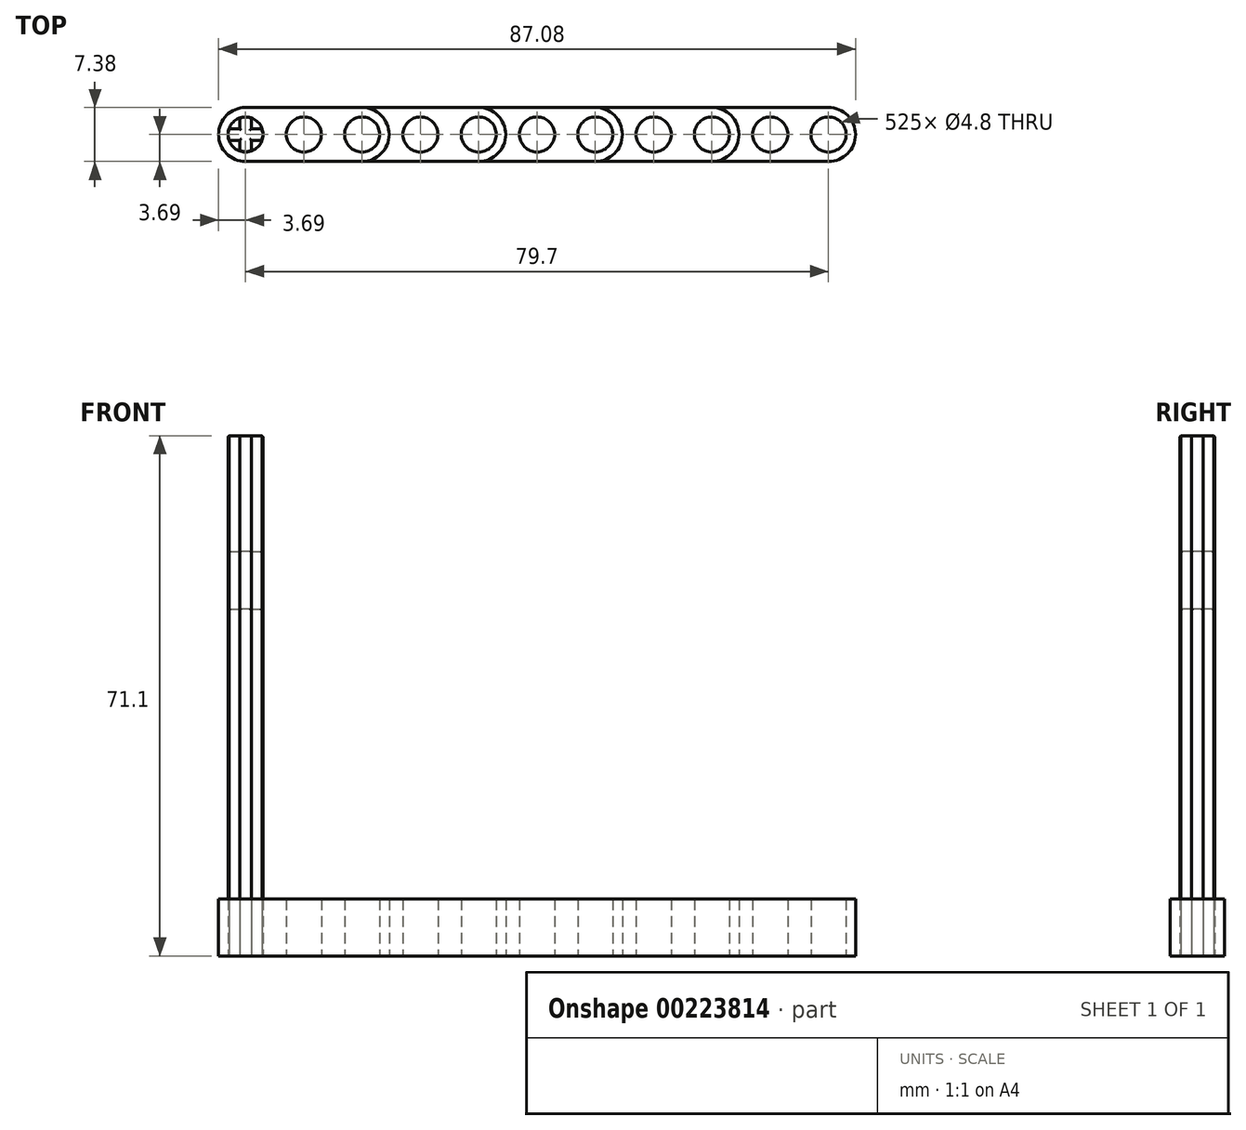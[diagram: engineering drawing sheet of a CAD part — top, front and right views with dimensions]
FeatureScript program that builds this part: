
annotation { "Feature Type Name" : "Feature", "Feature Type Description" : "" }
export const myFeature = defineFeature(function(context is Context, id is Id, definition is map)
    precondition{}
    {
        {
            var Q0;
            Q0=qCreatedBy(makeId("Top.planeOp"),FACE);
            var sketch = newSketch(context, id + "F0", { "sketchPlane" : qUnion([Q0])});
            skLineSegment(sketch, "E0", {"start": v(0, 0) * mm, "end": v(15.94, 0) * mm, "construction": true});
            skArc(sketch, "E1", {"start": v(15.94, -3.7) * mm, "mid": v(19.63, 0) * mm, "end": v(15.94, 3.69) * mm});
            skArc(sketch, "E2", {"start": v(0, 3.7) * mm, "mid": v(-3.7, 0) * mm, "end": v(0, -3.7) * mm});
            skLineSegment(sketch, "E3.MirrorCS", {"start": v(0, 3.69) * mm, "end": v(15.94, 3.69) * mm});
            skLineSegment(sketch, "E4.MirrorCS", {"start": v(0, -3.69) * mm, "end": v(15.94, -3.69) * mm});
            skCircle(sketch, "E5", {"center": v(0, 0) * mm, "radius": 2.4 * mm});
            skCircle(sketch, "E6.1.0.0", {"center": v(7.97, 0) * mm, "radius": 2.4 * mm});
            skCircle(sketch, "E6.2.0.0", {"center": v(15.94, 0) * mm, "radius": 2.4 * mm});
            skLineSegment(sketch, "E6.direction1", {"start": v(0, 0) * mm, "end": v(7.97, 0) * mm, "construction": true});
            skCircle(sketch, "E7", {"center": v(0, 0) * mm, "radius": 3.1 * mm});
            skCircle(sketch, "E8.1.0.0", {"center": v(7.97, 0) * mm, "radius": 3.1 * mm});
            skCircle(sketch, "E8.2.0.0", {"center": v(15.94, 0) * mm, "radius": 3.1 * mm});
            skSolve(sketch);
        }
        {
            var Q0;
            Q0=qCreatedBy(makeId("Top.planeOp"),FACE);
            var sketch = newSketch(context, id + "F1", { "sketchPlane" : qUnion([Q0])});
            skLineSegment(sketch, "E9", {"start": v(0, 0) * mm, "end": v(31.88, 0) * mm, "construction": true});
            skArc(sketch, "E10", {"start": v(31.88, -3.7) * mm, "mid": v(35.57, 0) * mm, "end": v(31.88, 3.7) * mm});
            skArc(sketch, "E11", {"start": v(0, 3.7) * mm, "mid": v(-3.7, 0) * mm, "end": v(0, -3.7) * mm});
            skLineSegment(sketch, "E12", {"start": v(0, 3.7) * mm, "end": v(31.88, 3.7) * mm});
            skLineSegment(sketch, "E13.MirrorCS", {"start": v(0, -3.7) * mm, "end": v(31.88, -3.7) * mm});
            skCircle(sketch, "E14", {"center": v(0, 0) * mm, "radius": 2.4 * mm});
            skCircle(sketch, "E15.1.0.0", {"center": v(7.97, 0) * mm, "radius": 2.4 * mm});
            skCircle(sketch, "E15.2.0.0", {"center": v(15.94, 0) * mm, "radius": 2.4 * mm});
            skCircle(sketch, "E15.3.0.0", {"center": v(23.91, 0) * mm, "radius": 2.4 * mm});
            skCircle(sketch, "E15.4.0.0", {"center": v(31.88, 0) * mm, "radius": 2.4 * mm});
            skLineSegment(sketch, "E15.direction1", {"start": v(0, 0) * mm, "end": v(7.97, 0) * mm, "construction": true});
            skSolve(sketch);
        }
        {
            var Q0;
            Q0=qCreatedBy(makeId("Top.planeOp"),FACE);
            var sketch = newSketch(context, id + "F17", { "sketchPlane" : qUnion([Q0])});
            skArc(sketch, "E16", {"start": v(47.82, -3.7) * mm, "mid": v(51.51, 0) * mm, "end": v(47.82, 3.7) * mm});
            skArc(sketch, "E17", {"start": v(0, 3.7) * mm, "mid": v(-3.7, 0) * mm, "end": v(0, -3.7) * mm});
            skLineSegment(sketch, "E18.MirrorCS", {"start": v(0, 3.7) * mm, "end": v(47.82, 3.7) * mm});
            skLineSegment(sketch, "E19.MirrorCS", {"start": v(0, -3.7) * mm, "end": v(47.82, -3.7) * mm});
            skCircle(sketch, "E20", {"center": v(0, 0) * mm, "radius": 2.4 * mm});
            skCircle(sketch, "E21.1.0.0", {"center": v(7.97, 0) * mm, "radius": 2.4 * mm});
            skCircle(sketch, "E21.2.0.0", {"center": v(15.94, 0) * mm, "radius": 2.4 * mm});
            skCircle(sketch, "E21.3.0.0", {"center": v(23.91, 0) * mm, "radius": 2.4 * mm});
            skCircle(sketch, "E21.4.0.0", {"center": v(31.88, 0) * mm, "radius": 2.4 * mm});
            skCircle(sketch, "E21.5.0.0", {"center": v(39.85, 0) * mm, "radius": 2.4 * mm});
            skCircle(sketch, "E21.6.0.0", {"center": v(47.82, 0) * mm, "radius": 2.4 * mm});
            skLineSegment(sketch, "E21.direction1", {"start": v(0, 0) * mm, "end": v(7.97, 0) * mm, "construction": true});
            skSolve(sketch);
        }
        {
            var Q0;
            Q0=qCreatedBy(makeId("Top.planeOp"),FACE);
            var sketch = newSketch(context, id + "F2", { "sketchPlane" : qUnion([Q0])});
            skLineSegment(sketch, "E22", {"start": v(0, 0) * mm, "end": v(63.76, 0) * mm, "construction": true});
            skArc(sketch, "E23", {"start": v(63.76, -3.7) * mm, "mid": v(67.45, 0) * mm, "end": v(63.76, 3.7) * mm});
            skArc(sketch, "E24", {"start": v(0, 3.7) * mm, "mid": v(-3.7, 0) * mm, "end": v(0, -3.7) * mm});
            skLineSegment(sketch, "E25", {"start": v(0, 3.7) * mm, "end": v(63.76, 3.7) * mm});
            skLineSegment(sketch, "E26.MirrorCS", {"start": v(0, -3.7) * mm, "end": v(63.76, -3.7) * mm});
            skCircle(sketch, "E27", {"center": v(0, 0) * mm, "radius": 2.4 * mm});
            skCircle(sketch, "E28.1.0.0", {"center": v(7.97, 0) * mm, "radius": 2.4 * mm});
            skCircle(sketch, "E28.2.0.0", {"center": v(15.94, 0) * mm, "radius": 2.4 * mm});
            skCircle(sketch, "E28.3.0.0", {"center": v(23.91, 0) * mm, "radius": 2.4 * mm});
            skCircle(sketch, "E28.4.0.0", {"center": v(31.88, 0) * mm, "radius": 2.4 * mm});
            skCircle(sketch, "E28.5.0.0", {"center": v(39.85, 0) * mm, "radius": 2.4 * mm});
            skCircle(sketch, "E28.6.0.0", {"center": v(47.82, 0) * mm, "radius": 2.4 * mm});
            skLineSegment(sketch, "E28.direction1", {"start": v(0, 0) * mm, "end": v(7.97, 0) * mm, "construction": true});
            skCircle(sketch, "E29.0.7.0", {"center": v(55.8, 0) * mm, "radius": 2.4 * mm});
            skCircle(sketch, "E29.0.8.0", {"center": v(63.76, 0) * mm, "radius": 2.4 * mm});
            skSolve(sketch);
        }
        {
            var Q0;
            Q0=qCreatedBy(makeId("Top.planeOp"),FACE);
            var sketch = newSketch(context, id + "F3", { "sketchPlane" : qUnion([Q0])});
            skLineSegment(sketch, "E30", {"start": v(0, 0) * mm, "end": v(79.7, 0) * mm, "construction": true});
            skArc(sketch, "E31", {"start": v(79.7, -3.7) * mm, "mid": v(83.4, 0) * mm, "end": v(79.7, 3.7) * mm});
            skArc(sketch, "E32", {"start": v(0, 3.7) * mm, "mid": v(-3.7, 0) * mm, "end": v(0, -3.7) * mm});
            skLineSegment(sketch, "E33", {"start": v(0, 3.7) * mm, "end": v(79.7, 3.7) * mm});
            skLineSegment(sketch, "E34.MirrorCS", {"start": v(0, -3.7) * mm, "end": v(79.7, -3.7) * mm});
            skCircle(sketch, "E35", {"center": v(0, 0) * mm, "radius": 2.4 * mm});
            skCircle(sketch, "E36.1.0.0", {"center": v(7.97, 0) * mm, "radius": 2.4 * mm});
            skCircle(sketch, "E36.2.0.0", {"center": v(15.94, 0) * mm, "radius": 2.4 * mm});
            skCircle(sketch, "E36.3.0.0", {"center": v(23.91, 0) * mm, "radius": 2.4 * mm});
            skCircle(sketch, "E36.4.0.0", {"center": v(31.88, 0) * mm, "radius": 2.4 * mm});
            skLineSegment(sketch, "E36.direction1", {"start": v(0, 0) * mm, "end": v(7.97, 0) * mm, "construction": true});
            skCircle(sketch, "E37.0.5.0", {"center": v(39.85, 0) * mm, "radius": 2.4 * mm});
            skCircle(sketch, "E37.0.6.0", {"center": v(47.82, 0) * mm, "radius": 2.4 * mm});
            skCircle(sketch, "E37.0.7.0", {"center": v(55.8, 0) * mm, "radius": 2.4 * mm});
            skCircle(sketch, "E37.0.8.0", {"center": v(63.76, 0) * mm, "radius": 2.4 * mm});
            skCircle(sketch, "E37.0.9.0", {"center": v(71.73, 0) * mm, "radius": 2.4 * mm});
            skCircle(sketch, "E37.0.10.0", {"center": v(79.7, 0) * mm, "radius": 2.4 * mm});
            skSolve(sketch);
        }
        {
            var Q0;
            Q0=qCreatedBy(makeId("Top.planeOp"),FACE);
            var sketch = newSketch(context, id + "F18", { "sketchPlane" : qUnion([Q0])});
            skArc(sketch, "E38", {"start": v(-0.8, -2.23) * mm, "mid": v(0, -2.37) * mm, "end": v(0.79, -2.23) * mm});
            skLineSegment(sketch, "E39", {"start": v(2.37, 0) * mm, "end": v(-2.37, 0) * mm, "construction": true});
            skLineSegment(sketch, "E40", {"start": v(0, 2.37) * mm, "end": v(0, -2.37) * mm, "construction": true});
            skLineSegment(sketch, "E41", {"start": v(-2.23, 0.79) * mm, "end": v(2.23, 0.79) * mm});
            skLineSegment(sketch, "E42", {"start": v(-2.23, -0.79) * mm, "end": v(2.23, -0.79) * mm});
            skLineSegment(sketch, "E43", {"start": v(-0.79, 2.23) * mm, "end": v(-0.8, -2.23) * mm});
            skLineSegment(sketch, "E44", {"start": v(0.8, 2.23) * mm, "end": v(0.8, 2.23) * mm});
            skLineSegment(sketch, "E45", {"start": v(0.79, 2.23) * mm, "end": v(0.8, -2.23) * mm});
            skArc(sketch, "E46.trimOffspring", {"start": v(-2.23, 0.79) * mm, "mid": v(-2.37, 0) * mm, "end": v(-2.23, -0.8) * mm});
            skArc(sketch, "E47.trimOffspring", {"start": v(0.79, 2.23) * mm, "mid": v(0, 2.37) * mm, "end": v(-0.79, 2.23) * mm});
            skArc(sketch, "E48.trimOffspring", {"start": v(2.23, -0.8) * mm, "mid": v(2.37, 0) * mm, "end": v(2.23, 0.79) * mm});
            skCircle(sketch, "E49", {"center": v(0, 0) * mm, "radius": 2.37 * mm, "construction": true});
            skSolve(sketch);
        }
        {
            var Q0;
            Q0=makeQuery(id+"F0.imprint","IMPRINT",FACE,{"disambiguationData":[TD([[makeQuery(id+"F0.imprint","IMPRINT",EDGE,{"derivedFrom":sQuery(id+"F0.wireOp",EDGE,"E5")}),-1.0]])]});
            var Q1;
            Q1=makeQuery(id+"F0.imprint","IMPRINT",FACE,{"disambiguationData":[TD([[makeQuery(id+"F0.imprint","IMPRINT",EDGE,{"derivedFrom":sQuery(id+"F0.wireOp",EDGE,"E6.1.0.0")}),-1.0]])]});
            var Q2;
            Q2=makeQuery(id+"F0.imprint","IMPRINT",FACE,{"disambiguationData":[TD([[makeQuery(id+"F0.imprint","IMPRINT",EDGE,{"derivedFrom":sQuery(id+"F0.wireOp",EDGE,"E6.2.0.0")}),-1.0]])]});
            var Q3;
            Q3=makeQuery(id+"F0.imprint","IMPRINT",FACE,{"disambiguationData":[TD([[makeQuery(id+"F0.imprint","IMPRINT",EDGE,{"derivedFrom":sQuery(id+"F0.wireOp",EDGE,"E1")}),1.0]])]});
            var Q4;
            Q4=makeQuery(id+"F19.opExtrude","CAP_FACE",FACE,{"disambiguationData":[OSD([sQuery(id+"F17.wireOp",EDGE,"E16"),sQuery(id+"F17.wireOp",EDGE,"E17"),sQuery(id+"F17.wireOp",EDGE,"E18.MirrorCS"),sQuery(id+"F17.wireOp",EDGE,"E19.MirrorCS"),sQuery(id+"F17.wireOp",EDGE,"E20"),sQuery(id+"F17.wireOp",EDGE,"E21.1.0.0"),sQuery(id+"F17.wireOp",EDGE,"E21.2.0.0"),sQuery(id+"F17.wireOp",EDGE,"E21.3.0.0"),sQuery(id+"F17.wireOp",EDGE,"E21.4.0.0"),sQuery(id+"F17.wireOp",EDGE,"E21.5.0.0"),sQuery(id+"F17.wireOp",EDGE,"E21.6.0.0")])],"isStart":false});
            extrude(context, id + "F4", {"entities" : qUnion([Q0, Q1, Q2, Q3]), "endBoundEntityFace" : qUnion([Q4]), "depth" : 7.76 * mm});
        }
        {
            var Q0;
            Q0 = qSketchRegion(id + "F1", true);
            var Q1;
            Q1=makeQuery(id+"F4.opExtrude","CAP_FACE",FACE,{"disambiguationData":[OSD([sQuery(id+"F0.wireOp",EDGE,"E1"),sQuery(id+"F0.wireOp",EDGE,"E2"),sQuery(id+"F0.wireOp",EDGE,"E3.MirrorCS"),sQuery(id+"F0.wireOp",EDGE,"E4.MirrorCS"),sQuery(id+"F0.wireOp",EDGE,"E5"),sQuery(id+"F0.wireOp",EDGE,"E6.1.0.0"),sQuery(id+"F0.wireOp",EDGE,"E6.2.0.0")])],"isStart":false});
            extrude(context, id + "F5", {"entities" : qUnion([Q0]), "endBound" : BoundingType.UP_TO_SURFACE, "endBoundEntityFace" : qUnion([Q1]), "depth" : 8 * mm});
        }
        {
            var Q0;
            Q0 = qSketchRegion(id + "F17", true);
            var Q1;
            Q1=makeQuery(id+"F4.opExtrude","CAP_FACE",FACE,{"disambiguationData":[OSD([sQuery(id+"F0.wireOp",EDGE,"E1"),sQuery(id+"F0.wireOp",EDGE,"E2"),sQuery(id+"F0.wireOp",EDGE,"E3.MirrorCS"),sQuery(id+"F0.wireOp",EDGE,"E4.MirrorCS"),sQuery(id+"F0.wireOp",EDGE,"E5"),sQuery(id+"F0.wireOp",EDGE,"E6.1.0.0"),sQuery(id+"F0.wireOp",EDGE,"E6.2.0.0")])],"isStart":false});
            extrude(context, id + "F19", {"entities" : qUnion([Q0]), "endBound" : BoundingType.UP_TO_SURFACE, "endBoundEntityFace" : qUnion([Q1]), "depth" : 7.8 * mm});
        }
        {
            var Q0;
            Q0 = qSketchRegion(id + "F2", true);
            var Q1;
            Q1=makeQuery(id+"F4.opExtrude","CAP_FACE",FACE,{"disambiguationData":[OSD([sQuery(id+"F0.wireOp",EDGE,"E1"),sQuery(id+"F0.wireOp",EDGE,"E2"),sQuery(id+"F0.wireOp",EDGE,"E3.MirrorCS"),sQuery(id+"F0.wireOp",EDGE,"E4.MirrorCS"),sQuery(id+"F0.wireOp",EDGE,"E5"),sQuery(id+"F0.wireOp",EDGE,"E6.1.0.0"),sQuery(id+"F0.wireOp",EDGE,"E6.2.0.0")])],"isStart":false});
            extrude(context, id + "F20", {"entities" : qUnion([Q0]), "endBound" : BoundingType.UP_TO_SURFACE, "endBoundEntityFace" : qUnion([Q1]), "depth" : 8 * mm});
        }
        {
            var Q0;
            Q0=makeQuery(id+"F3.imprint","IMPRINT",FACE,{"disambiguationData":[TD([[makeQuery(id+"F3.imprint","IMPRINT",EDGE,{"derivedFrom":sQuery(id+"F3.wireOp",EDGE,"E31")}),1.0]])]});
            var Q1;
            Q1=makeQuery(id+"F4.opExtrude","CAP_FACE",FACE,{"disambiguationData":[OSD([sQuery(id+"F0.wireOp",EDGE,"E1"),sQuery(id+"F0.wireOp",EDGE,"E2"),sQuery(id+"F0.wireOp",EDGE,"E3.MirrorCS"),sQuery(id+"F0.wireOp",EDGE,"E4.MirrorCS"),sQuery(id+"F0.wireOp",EDGE,"E5"),sQuery(id+"F0.wireOp",EDGE,"E6.1.0.0"),sQuery(id+"F0.wireOp",EDGE,"E6.2.0.0")])],"isStart":false});
            extrude(context, id + "F6", {"entities" : qUnion([Q0]), "endBound" : BoundingType.UP_TO_SURFACE, "endBoundEntityFace" : qUnion([Q1]), "depth" : 25 * mm});
        }
        {
            var Q0;
            Q0 = qSketchRegion(id + "F18", true);
            extrude(context, id + "F7", {"entities" : qUnion([Q0]), "depth" : 2 * 7.9 * mm});
        }
        {
            var Q0;
            Q0=makeQuery(id+"F7.opExtrude","CAP_FACE",FACE,{"disambiguationData":[OSD([sQuery(id+"F18.wireOp",EDGE,"E38"),sQuery(id+"F18.wireOp",EDGE,"E41"),sQuery(id+"F18.wireOp",EDGE,"E42"),sQuery(id+"F18.wireOp",EDGE,"E43"),sQuery(id+"F18.wireOp",EDGE,"E45"),sQuery(id+"F18.wireOp",EDGE,"E46.trimOffspring"),sQuery(id+"F18.wireOp",EDGE,"E47.trimOffspring"),sQuery(id+"F18.wireOp",EDGE,"E48.trimOffspring")])],"isStart":false});
            var Q1;
            Q1=makeQuery(id+"F7.opExtrude","CAP_FACE",FACE,{"disambiguationData":[OSD([sQuery(id+"F18.wireOp",EDGE,"E38"),sQuery(id+"F18.wireOp",EDGE,"E41"),sQuery(id+"F18.wireOp",EDGE,"E42"),sQuery(id+"F18.wireOp",EDGE,"E43"),sQuery(id+"F18.wireOp",EDGE,"E45"),sQuery(id+"F18.wireOp",EDGE,"E46.trimOffspring"),sQuery(id+"F18.wireOp",EDGE,"E47.trimOffspring"),sQuery(id+"F18.wireOp",EDGE,"E48.trimOffspring")])],"isStart":true});
            fillet(context, id + "F21", {"entities" : qUnion([Q0, Q1]), "radius" : 0.2 * mm, "tangentPropagation" : true, "allowEdgeOverflow" : false});
        }
        {
            var Q0;
            Q0 = qSketchRegion(id + "F18", true);
            extrude(context, id + "F8", {"entities" : qUnion([Q0]), "depth" : 3 * 7.9 * mm});
        }
        {
            var Q0;
            Q0=makeQuery(id+"F8.opExtrude","CAP_FACE",FACE,{"disambiguationData":[OSD([sQuery(id+"F18.wireOp",EDGE,"E38"),sQuery(id+"F18.wireOp",EDGE,"E41"),sQuery(id+"F18.wireOp",EDGE,"E42"),sQuery(id+"F18.wireOp",EDGE,"E43"),sQuery(id+"F18.wireOp",EDGE,"E45"),sQuery(id+"F18.wireOp",EDGE,"E46.trimOffspring"),sQuery(id+"F18.wireOp",EDGE,"E47.trimOffspring"),sQuery(id+"F18.wireOp",EDGE,"E48.trimOffspring")])],"isStart":true});
            fillet(context, id + "F9", {"entities" : qUnion([Q0]), "radius" : 0.2 * mm, "tangentPropagation" : true, "allowEdgeOverflow" : false});
        }
        {
            var Q0;
            Q0 = qSketchRegion(id + "F18", true);
            extrude(context, id + "F22", {"entities" : qUnion([Q0]), "depth" : 4 * 7.9 * mm});
        }
        {
            var Q0;
            Q0=makeQuery(id+"F22.opExtrude","CAP_FACE",FACE,{"disambiguationData":[OSD([sQuery(id+"F18.wireOp",EDGE,"E38"),sQuery(id+"F18.wireOp",EDGE,"E41"),sQuery(id+"F18.wireOp",EDGE,"E42"),sQuery(id+"F18.wireOp",EDGE,"E43"),sQuery(id+"F18.wireOp",EDGE,"E45"),sQuery(id+"F18.wireOp",EDGE,"E46.trimOffspring"),sQuery(id+"F18.wireOp",EDGE,"E47.trimOffspring"),sQuery(id+"F18.wireOp",EDGE,"E48.trimOffspring")])],"isStart":true});
            var Q1;
            Q1=makeQuery(id+"F22.opExtrude","CAP_FACE",FACE,{"disambiguationData":[OSD([sQuery(id+"F18.wireOp",EDGE,"E38"),sQuery(id+"F18.wireOp",EDGE,"E41"),sQuery(id+"F18.wireOp",EDGE,"E42"),sQuery(id+"F18.wireOp",EDGE,"E43"),sQuery(id+"F18.wireOp",EDGE,"E45"),sQuery(id+"F18.wireOp",EDGE,"E46.trimOffspring"),sQuery(id+"F18.wireOp",EDGE,"E47.trimOffspring"),sQuery(id+"F18.wireOp",EDGE,"E48.trimOffspring")])],"isStart":false});
            fillet(context, id + "F10", {"entities" : qUnion([Q0, Q1]), "radius" : 0.2 * mm, "tangentPropagation" : true, "allowEdgeOverflow" : false});
        }
        {
            var Q0;
            Q0 = qSketchRegion(id + "F18", true);
            extrude(context, id + "F23", {"entities" : qUnion([Q0]), "operationType" : NewBodyOperationType.ADD, "depth" : 5 * 7.9 * mm});
        }
        {
            var Q0;
            Q0=makeQuery(id+"F23.opExtrude","CAP_FACE",FACE,{"disambiguationData":[OSD([sQuery(id+"F18.wireOp",EDGE,"E38"),sQuery(id+"F18.wireOp",EDGE,"E41"),sQuery(id+"F18.wireOp",EDGE,"E42"),sQuery(id+"F18.wireOp",EDGE,"E43"),sQuery(id+"F18.wireOp",EDGE,"E45"),sQuery(id+"F18.wireOp",EDGE,"E46.trimOffspring"),sQuery(id+"F18.wireOp",EDGE,"E47.trimOffspring"),sQuery(id+"F18.wireOp",EDGE,"E48.trimOffspring")])],"isStart":false});
            var Q1;
            {var subQ0=sQuery(id+"F18.wireOp",EDGE,"E48.trimOffspring");var subQ1=sQuery(id+"F18.wireOp",EDGE,"E47.trimOffspring");var subQ2=sQuery(id+"F18.wireOp",EDGE,"E46.trimOffspring");var subQ3=sQuery(id+"F18.wireOp",EDGE,"E45");var subQ4=sQuery(id+"F18.wireOp",EDGE,"E43");var subQ5=sQuery(id+"F18.wireOp",EDGE,"E42");var subQ6=sQuery(id+"F18.wireOp",EDGE,"E41");var subQ7=sQuery(id+"F18.wireOp",EDGE,"E38");Q1=makeQuery(id+"F23.boolean.opBoolean","MERGE",FACE,{"derivedFrom":[makeQuery(id+"F22.opExtrude","CAP_FACE",FACE,{"disambiguationData":[OSD([subQ7,subQ6,subQ5,subQ4,subQ3,subQ2,subQ1,subQ0])],"isStart":true}),makeQuery(id+"F23.opExtrude","CAP_FACE",FACE,{"disambiguationData":[OSD([subQ7,subQ6,subQ5,subQ4,subQ3,subQ2,subQ1,subQ0])],"isStart":true})]});}
            fillet(context, id + "F11", {"entities" : qUnion([Q0, Q1]), "radius" : 0.2 * mm, "tangentPropagation" : true, "allowEdgeOverflow" : false});
        }
        {
            var Q0;
            Q0 = qSketchRegion(id + "F18", true);
            extrude(context, id + "F12", {"entities" : qUnion([Q0]), "depth" : 7 * 7.9 * mm});
        }
        {
            var Q0;
            Q0=makeQuery(id+"F12.opExtrude","CAP_FACE",FACE,{"disambiguationData":[OSD([sQuery(id+"F18.wireOp",EDGE,"E38"),sQuery(id+"F18.wireOp",EDGE,"E41"),sQuery(id+"F18.wireOp",EDGE,"E42"),sQuery(id+"F18.wireOp",EDGE,"E43"),sQuery(id+"F18.wireOp",EDGE,"E45"),sQuery(id+"F18.wireOp",EDGE,"E46.trimOffspring"),sQuery(id+"F18.wireOp",EDGE,"E47.trimOffspring"),sQuery(id+"F18.wireOp",EDGE,"E48.trimOffspring")])],"isStart":true});
            var Q1;
            Q1=makeQuery(id+"F12.opExtrude","CAP_FACE",FACE,{"disambiguationData":[OSD([sQuery(id+"F18.wireOp",EDGE,"E38"),sQuery(id+"F18.wireOp",EDGE,"E41"),sQuery(id+"F18.wireOp",EDGE,"E42"),sQuery(id+"F18.wireOp",EDGE,"E43"),sQuery(id+"F18.wireOp",EDGE,"E45"),sQuery(id+"F18.wireOp",EDGE,"E46.trimOffspring"),sQuery(id+"F18.wireOp",EDGE,"E47.trimOffspring"),sQuery(id+"F18.wireOp",EDGE,"E48.trimOffspring")])],"isStart":false});
            fillet(context, id + "F13", {"entities" : qUnion([Q0, Q1]), "radius" : 0.2 * mm, "tangentPropagation" : true, "allowEdgeOverflow" : false});
        }
        {
            var Q0;
            Q0 = qSketchRegion(id + "F18", true);
            extrude(context, id + "F14", {"entities" : qUnion([Q0]), "depth" : 9 * 7.9 * mm});
        }
        {
            var Q0;
            Q0=makeQuery(id+"F14.opExtrude","CAP_FACE",FACE,{"disambiguationData":[OSD([sQuery(id+"F18.wireOp",EDGE,"E38"),sQuery(id+"F18.wireOp",EDGE,"E41"),sQuery(id+"F18.wireOp",EDGE,"E42"),sQuery(id+"F18.wireOp",EDGE,"E43"),sQuery(id+"F18.wireOp",EDGE,"E45"),sQuery(id+"F18.wireOp",EDGE,"E46.trimOffspring"),sQuery(id+"F18.wireOp",EDGE,"E47.trimOffspring"),sQuery(id+"F18.wireOp",EDGE,"E48.trimOffspring")])],"isStart":true});
            var Q1;
            Q1=makeQuery(id+"F14.opExtrude","CAP_FACE",FACE,{"disambiguationData":[OSD([sQuery(id+"F18.wireOp",EDGE,"E38"),sQuery(id+"F18.wireOp",EDGE,"E41"),sQuery(id+"F18.wireOp",EDGE,"E42"),sQuery(id+"F18.wireOp",EDGE,"E43"),sQuery(id+"F18.wireOp",EDGE,"E45"),sQuery(id+"F18.wireOp",EDGE,"E46.trimOffspring"),sQuery(id+"F18.wireOp",EDGE,"E47.trimOffspring"),sQuery(id+"F18.wireOp",EDGE,"E48.trimOffspring")])],"isStart":false});
            fillet(context, id + "F24", {"entities" : qUnion([Q0, Q1]), "radius" : 0.2 * mm, "tangentPropagation" : true, "allowEdgeOverflow" : false});
        }
        {
            var Q0;
            Q0 = qSketchRegion(id + "F18", true);
            extrude(context, id + "F15", {"entities" : qUnion([Q0]), "depth" : 6 * 7.9 * mm});
        }
        {
            var Q0;
            Q0=makeQuery(id+"F15.opExtrude","CAP_FACE",FACE,{"disambiguationData":[OSD([sQuery(id+"F18.wireOp",EDGE,"E38"),sQuery(id+"F18.wireOp",EDGE,"E41"),sQuery(id+"F18.wireOp",EDGE,"E42"),sQuery(id+"F18.wireOp",EDGE,"E43"),sQuery(id+"F18.wireOp",EDGE,"E45"),sQuery(id+"F18.wireOp",EDGE,"E46.trimOffspring"),sQuery(id+"F18.wireOp",EDGE,"E47.trimOffspring"),sQuery(id+"F18.wireOp",EDGE,"E48.trimOffspring")])],"isStart":false});
            var Q1;
            Q1=makeQuery(id+"F15.opExtrude","CAP_FACE",FACE,{"disambiguationData":[OSD([sQuery(id+"F18.wireOp",EDGE,"E38"),sQuery(id+"F18.wireOp",EDGE,"E41"),sQuery(id+"F18.wireOp",EDGE,"E42"),sQuery(id+"F18.wireOp",EDGE,"E43"),sQuery(id+"F18.wireOp",EDGE,"E45"),sQuery(id+"F18.wireOp",EDGE,"E46.trimOffspring"),sQuery(id+"F18.wireOp",EDGE,"E47.trimOffspring"),sQuery(id+"F18.wireOp",EDGE,"E48.trimOffspring")])],"isStart":true});
            fillet(context, id + "F16", {"entities" : qUnion([Q0, Q1]), "radius" : 0.2 * mm, "tangentPropagation" : true, "allowEdgeOverflow" : false});
        }
    });
